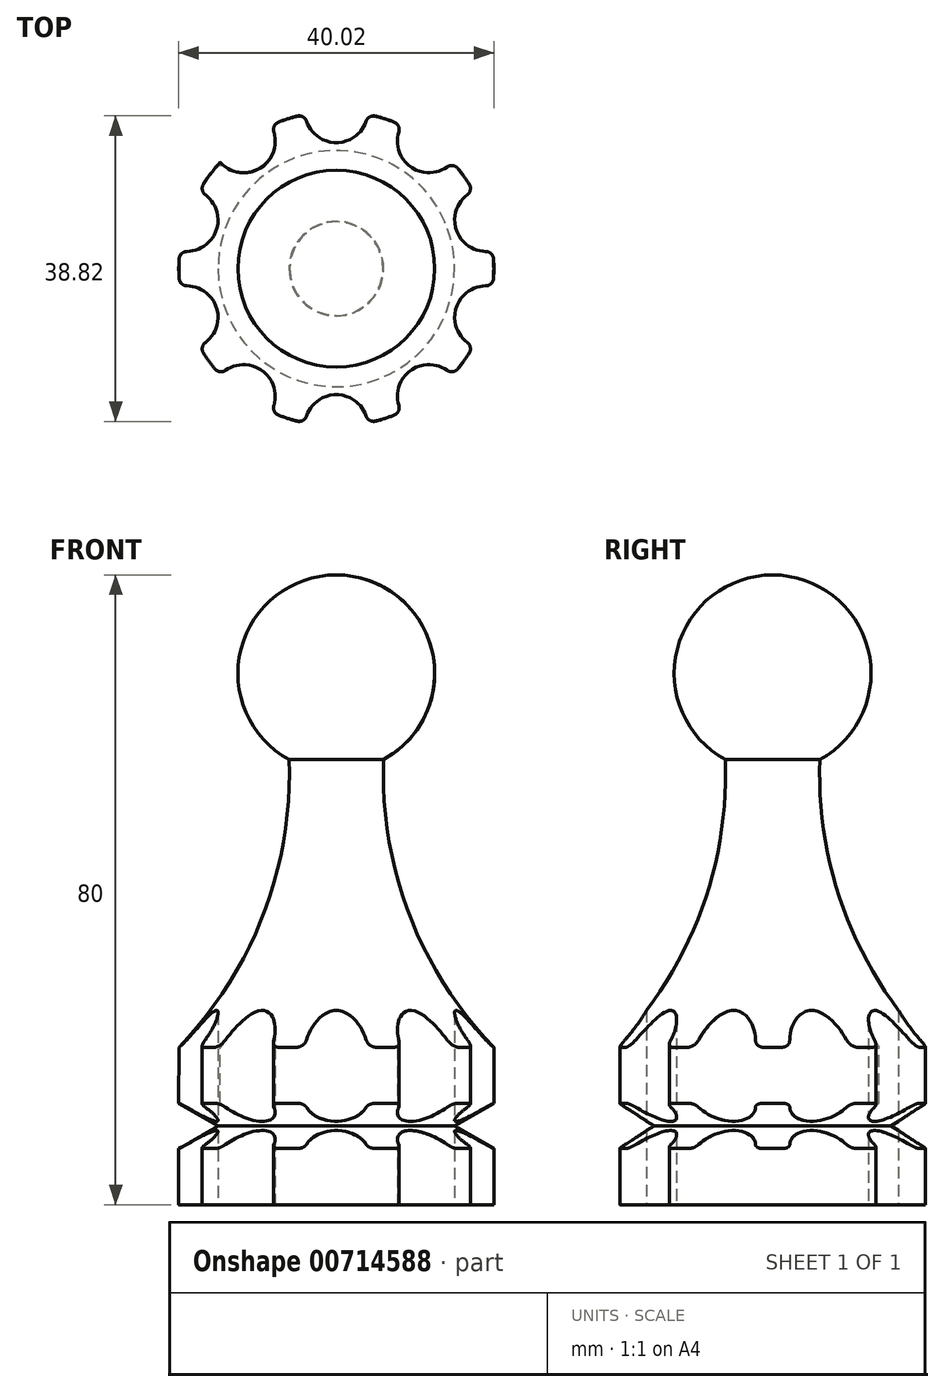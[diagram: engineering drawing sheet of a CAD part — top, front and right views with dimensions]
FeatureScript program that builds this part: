
annotation { "Feature Type Name" : "Feature", "Feature Type Description" : "" }
export const myFeature = defineFeature(function(context is Context, id is Id, definition is map)
    precondition{}
    {
        {
            var Q0;
            Q0=qCreatedBy(makeId("Front.planeOp"),FACE);
            var sketch = newSketch(context, id + "F0", { "sketchPlane" : qUnion([Q0])});
            skLineSegment(sketch, "E0", {"start": v(0, 0) * mm, "end": v(0, 80) * mm});
            skLineSegment(sketch, "E1", {"start": v(0, 0) * mm, "end": v(20, 0) * mm});
            skArc(sketch, "E2", {"start": v(6, 56.53) * mm, "mid": v(9.28, 36.84) * mm, "end": v(20, 20) * mm});
            skArc(sketch, "E3", {"start": v(6, 56.53) * mm, "mid": v(12.11, 70.6) * mm, "end": v(0, 80) * mm});
            skLineSegment(sketch, "E4", {"start": v(20, 0) * mm, "end": v(20, 7.12) * mm});
            skLineSegment(sketch, "E5", {"start": v(20, 7.12) * mm, "end": v(15, 10) * mm});
            skLineSegment(sketch, "E6", {"start": v(15, 10) * mm, "end": v(20, 12.9) * mm});
            skLineSegment(sketch, "E7", {"start": v(20, 12.9) * mm, "end": v(20, 20) * mm});
            skSolve(sketch);
        }
        {
            var Q0;
            Q0 = qSketchRegion(id + "F0", true);
            var Q1;
            Q1=sQuery(id+"F0.wireOp",EDGE,"E0");
            revolve(context, id + "F1", {"surfaceOperationType" : NewSurfaceOperationType.NEW, "entities" : qUnion([Q0]), "axis" : qUnion([Q1]), "revolveType" : RevolveType.FULL});
        }
        {
            var Q0;
            Q0=makeQuery(id+"F1.opRevolve","SWEPT_FACE",FACE,{"disambiguationData":[OSD([sQuery(id+"F0.wireOp",EDGE,"E1")])]});
            var sketch = newSketch(context, id + "F2", { "sketchPlane" : qUnion([Q0])});
            skCircle(sketch, "E8", {"center": v(0, 20) * mm, "radius": 4 * mm});
            skCircle(sketch, "E9.1.0", {"center": v(-11.76, 16.19) * mm, "radius": 4 * mm});
            skCircle(sketch, "E9.2.0", {"center": v(-19.03, 6.18) * mm, "radius": 4 * mm});
            skCircle(sketch, "E9.3.0", {"center": v(-19.03, -6.18) * mm, "radius": 4 * mm});
            skCircle(sketch, "E9.4.0", {"center": v(-11.76, -16.19) * mm, "radius": 4 * mm});
            skCircle(sketch, "E9.5.0", {"center": v(0, -20) * mm, "radius": 4 * mm});
            skCircle(sketch, "E9.6.0", {"center": v(11.76, -16.19) * mm, "radius": 4 * mm});
            skCircle(sketch, "E9.7.0", {"center": v(19.03, -6.18) * mm, "radius": 4 * mm});
            skCircle(sketch, "E9.8.0", {"center": v(19.03, 6.18) * mm, "radius": 4 * mm});
            skCircle(sketch, "E9.9.0", {"center": v(11.76, 16.19) * mm, "radius": 4 * mm});
            skPoint(sketch, "E9.center", {"position": v(0, 0) * mm});
            skSolve(sketch);
        }
        {
            var Q0;
            Q0 = qSketchRegion(id + "F2", true);
            extrude(context, id + "F3", {"entities" : qUnion([Q0]), "operationType" : NewBodyOperationType.REMOVE, "oppositeDirection" : true, "depth" : 25 * mm, "offsetDistance" : 25 * mm});
        }
        {
            var Q0;
            Q0=makeQuery(id+"F3.boolean.opBoolean","INTERSECT",EDGE,{"disambiguationData":[OD(1.0)],"derivedFrom":[makeQuery(id+"F1.opRevolve","SWEPT_FACE",FACE,{"disambiguationData":[OSD([sQuery(id+"F0.wireOp",EDGE,"E7")])]}),makeQuery(id+"F3.opExtrude","SWEPT_FACE",FACE,{"disambiguationData":[OSD([sQuery(id+"F2.wireOp",EDGE,"E9.1.0")])]})]});
            var Q1;
            Q1=makeQuery(id+"F3.boolean.opBoolean","INTERSECT",EDGE,{"disambiguationData":[OD(0.0)],"derivedFrom":[makeQuery(id+"F1.opRevolve","SWEPT_FACE",FACE,{"disambiguationData":[OSD([sQuery(id+"F0.wireOp",EDGE,"E7")])]}),makeQuery(id+"F3.opExtrude","SWEPT_FACE",FACE,{"disambiguationData":[OSD([sQuery(id+"F2.wireOp",EDGE,"E9.1.0")])]})]});
            var Q2;
            Q2=makeQuery(id+"F3.boolean.opBoolean","INTERSECT",EDGE,{"disambiguationData":[OD(1.0)],"derivedFrom":[makeQuery(id+"F1.opRevolve","SWEPT_FACE",FACE,{"disambiguationData":[OSD([sQuery(id+"F0.wireOp",EDGE,"E7")])]}),makeQuery(id+"F3.opExtrude","SWEPT_FACE",FACE,{"disambiguationData":[OSD([sQuery(id+"F2.wireOp",EDGE,"E8")])]})]});
            var Q3;
            Q3=makeQuery(id+"F3.boolean.opBoolean","INTERSECT",EDGE,{"disambiguationData":[OD(0.0)],"derivedFrom":[makeQuery(id+"F1.opRevolve","SWEPT_FACE",FACE,{"disambiguationData":[OSD([sQuery(id+"F0.wireOp",EDGE,"E7")])]}),makeQuery(id+"F3.opExtrude","SWEPT_FACE",FACE,{"disambiguationData":[OSD([sQuery(id+"F2.wireOp",EDGE,"E8")])]})]});
            var Q4;
            Q4=makeQuery(id+"F3.boolean.opBoolean","INTERSECT",EDGE,{"disambiguationData":[OD(0.0)],"derivedFrom":[makeQuery(id+"F1.opRevolve","SWEPT_FACE",FACE,{"disambiguationData":[OSD([sQuery(id+"F0.wireOp",EDGE,"E7")])]}),makeQuery(id+"F3.opExtrude","SWEPT_FACE",FACE,{"disambiguationData":[OSD([sQuery(id+"F2.wireOp",EDGE,"E9.9.0")])]})]});
            var Q5;
            Q5=makeQuery(id+"F3.boolean.opBoolean","INTERSECT",EDGE,{"disambiguationData":[OD(1.0)],"derivedFrom":[makeQuery(id+"F1.opRevolve","SWEPT_FACE",FACE,{"disambiguationData":[OSD([sQuery(id+"F0.wireOp",EDGE,"E7")])]}),makeQuery(id+"F3.opExtrude","SWEPT_FACE",FACE,{"disambiguationData":[OSD([sQuery(id+"F2.wireOp",EDGE,"E9.9.0")])]})]});
            var Q6;
            Q6=makeQuery(id+"F3.boolean.opBoolean","INTERSECT",EDGE,{"disambiguationData":[OD(1.0)],"derivedFrom":[makeQuery(id+"F1.opRevolve","SWEPT_FACE",FACE,{"disambiguationData":[OSD([sQuery(id+"F0.wireOp",EDGE,"E7")])]}),makeQuery(id+"F3.opExtrude","SWEPT_FACE",FACE,{"disambiguationData":[OSD([sQuery(id+"F2.wireOp",EDGE,"E9.8.0")])]})]});
            var Q7;
            Q7=makeQuery(id+"F3.boolean.opBoolean","INTERSECT",EDGE,{"disambiguationData":[OD(0.0)],"derivedFrom":[makeQuery(id+"F1.opRevolve","SWEPT_FACE",FACE,{"disambiguationData":[OSD([sQuery(id+"F0.wireOp",EDGE,"E7")])]}),makeQuery(id+"F3.opExtrude","SWEPT_FACE",FACE,{"disambiguationData":[OSD([sQuery(id+"F2.wireOp",EDGE,"E9.8.0")])]})]});
            var Q8;
            Q8=makeQuery(id+"F3.boolean.opBoolean","INTERSECT",EDGE,{"disambiguationData":[OD(1.0)],"derivedFrom":[makeQuery(id+"F1.opRevolve","SWEPT_FACE",FACE,{"disambiguationData":[OSD([sQuery(id+"F0.wireOp",EDGE,"E7")])]}),makeQuery(id+"F3.opExtrude","SWEPT_FACE",FACE,{"disambiguationData":[OSD([sQuery(id+"F2.wireOp",EDGE,"E9.7.0")])]})]});
            var Q9;
            Q9=makeQuery(id+"F3.boolean.opBoolean","INTERSECT",EDGE,{"disambiguationData":[OD(0.0)],"derivedFrom":[makeQuery(id+"F1.opRevolve","SWEPT_FACE",FACE,{"disambiguationData":[OSD([sQuery(id+"F0.wireOp",EDGE,"E7")])]}),makeQuery(id+"F3.opExtrude","SWEPT_FACE",FACE,{"disambiguationData":[OSD([sQuery(id+"F2.wireOp",EDGE,"E9.7.0")])]})]});
            var Q10;
            Q10=makeQuery(id+"F3.boolean.opBoolean","INTERSECT",EDGE,{"disambiguationData":[OD(1.0)],"derivedFrom":[makeQuery(id+"F1.opRevolve","SWEPT_FACE",FACE,{"disambiguationData":[OSD([sQuery(id+"F0.wireOp",EDGE,"E7")])]}),makeQuery(id+"F3.opExtrude","SWEPT_FACE",FACE,{"disambiguationData":[OSD([sQuery(id+"F2.wireOp",EDGE,"E9.6.0")])]})]});
            var Q11;
            Q11=makeQuery(id+"F3.boolean.opBoolean","INTERSECT",EDGE,{"disambiguationData":[OD(0.0)],"derivedFrom":[makeQuery(id+"F1.opRevolve","SWEPT_FACE",FACE,{"disambiguationData":[OSD([sQuery(id+"F0.wireOp",EDGE,"E7")])]}),makeQuery(id+"F3.opExtrude","SWEPT_FACE",FACE,{"disambiguationData":[OSD([sQuery(id+"F2.wireOp",EDGE,"E9.6.0")])]})]});
            var Q12;
            Q12=makeQuery(id+"F3.boolean.opBoolean","INTERSECT",EDGE,{"disambiguationData":[OD(1.0)],"derivedFrom":[makeQuery(id+"F1.opRevolve","SWEPT_FACE",FACE,{"disambiguationData":[OSD([sQuery(id+"F0.wireOp",EDGE,"E4")])]}),makeQuery(id+"F3.opExtrude","SWEPT_FACE",FACE,{"disambiguationData":[OSD([sQuery(id+"F2.wireOp",EDGE,"E9.1.0")])]})]});
            var Q13;
            Q13=makeQuery(id+"F3.boolean.opBoolean","INTERSECT",EDGE,{"disambiguationData":[OD(0.0)],"derivedFrom":[makeQuery(id+"F1.opRevolve","SWEPT_FACE",FACE,{"disambiguationData":[OSD([sQuery(id+"F0.wireOp",EDGE,"E4")])]}),makeQuery(id+"F3.opExtrude","SWEPT_FACE",FACE,{"disambiguationData":[OSD([sQuery(id+"F2.wireOp",EDGE,"E9.1.0")])]})]});
            var Q14;
            Q14=makeQuery(id+"F3.boolean.opBoolean","INTERSECT",EDGE,{"disambiguationData":[OD(0.0)],"derivedFrom":[makeQuery(id+"F1.opRevolve","SWEPT_FACE",FACE,{"disambiguationData":[OSD([sQuery(id+"F0.wireOp",EDGE,"E4")])]}),makeQuery(id+"F3.opExtrude","SWEPT_FACE",FACE,{"disambiguationData":[OSD([sQuery(id+"F2.wireOp",EDGE,"E8")])]})]});
            var Q15;
            Q15=makeQuery(id+"F3.boolean.opBoolean","INTERSECT",EDGE,{"disambiguationData":[OD(1.0)],"derivedFrom":[makeQuery(id+"F1.opRevolve","SWEPT_FACE",FACE,{"disambiguationData":[OSD([sQuery(id+"F0.wireOp",EDGE,"E4")])]}),makeQuery(id+"F3.opExtrude","SWEPT_FACE",FACE,{"disambiguationData":[OSD([sQuery(id+"F2.wireOp",EDGE,"E8")])]})]});
            var Q16;
            Q16=makeQuery(id+"F3.boolean.opBoolean","INTERSECT",EDGE,{"disambiguationData":[OD(0.0)],"derivedFrom":[makeQuery(id+"F1.opRevolve","SWEPT_FACE",FACE,{"disambiguationData":[OSD([sQuery(id+"F0.wireOp",EDGE,"E4")])]}),makeQuery(id+"F3.opExtrude","SWEPT_FACE",FACE,{"disambiguationData":[OSD([sQuery(id+"F2.wireOp",EDGE,"E9.9.0")])]})]});
            var Q17;
            Q17=makeQuery(id+"F3.boolean.opBoolean","INTERSECT",EDGE,{"disambiguationData":[OD(1.0)],"derivedFrom":[makeQuery(id+"F1.opRevolve","SWEPT_FACE",FACE,{"disambiguationData":[OSD([sQuery(id+"F0.wireOp",EDGE,"E4")])]}),makeQuery(id+"F3.opExtrude","SWEPT_FACE",FACE,{"disambiguationData":[OSD([sQuery(id+"F2.wireOp",EDGE,"E9.9.0")])]})]});
            var Q18;
            Q18=makeQuery(id+"F3.boolean.opBoolean","INTERSECT",EDGE,{"disambiguationData":[OD(1.0)],"derivedFrom":[makeQuery(id+"F1.opRevolve","SWEPT_FACE",FACE,{"disambiguationData":[OSD([sQuery(id+"F0.wireOp",EDGE,"E4")])]}),makeQuery(id+"F3.opExtrude","SWEPT_FACE",FACE,{"disambiguationData":[OSD([sQuery(id+"F2.wireOp",EDGE,"E9.8.0")])]})]});
            var Q19;
            Q19=makeQuery(id+"F3.boolean.opBoolean","INTERSECT",EDGE,{"disambiguationData":[OD(0.0)],"derivedFrom":[makeQuery(id+"F1.opRevolve","SWEPT_FACE",FACE,{"disambiguationData":[OSD([sQuery(id+"F0.wireOp",EDGE,"E4")])]}),makeQuery(id+"F3.opExtrude","SWEPT_FACE",FACE,{"disambiguationData":[OSD([sQuery(id+"F2.wireOp",EDGE,"E9.8.0")])]})]});
            var Q20;
            Q20=makeQuery(id+"F3.boolean.opBoolean","INTERSECT",EDGE,{"disambiguationData":[OD(1.0)],"derivedFrom":[makeQuery(id+"F1.opRevolve","SWEPT_FACE",FACE,{"disambiguationData":[OSD([sQuery(id+"F0.wireOp",EDGE,"E4")])]}),makeQuery(id+"F3.opExtrude","SWEPT_FACE",FACE,{"disambiguationData":[OSD([sQuery(id+"F2.wireOp",EDGE,"E9.7.0")])]})]});
            var Q21;
            Q21=makeQuery(id+"F3.boolean.opBoolean","INTERSECT",EDGE,{"disambiguationData":[OD(0.0)],"derivedFrom":[makeQuery(id+"F1.opRevolve","SWEPT_FACE",FACE,{"disambiguationData":[OSD([sQuery(id+"F0.wireOp",EDGE,"E4")])]}),makeQuery(id+"F3.opExtrude","SWEPT_FACE",FACE,{"disambiguationData":[OSD([sQuery(id+"F2.wireOp",EDGE,"E9.7.0")])]})]});
            var Q22;
            Q22=makeQuery(id+"F3.boolean.opBoolean","INTERSECT",EDGE,{"disambiguationData":[OD(1.0)],"derivedFrom":[makeQuery(id+"F1.opRevolve","SWEPT_FACE",FACE,{"disambiguationData":[OSD([sQuery(id+"F0.wireOp",EDGE,"E4")])]}),makeQuery(id+"F3.opExtrude","SWEPT_FACE",FACE,{"disambiguationData":[OSD([sQuery(id+"F2.wireOp",EDGE,"E9.6.0")])]})]});
            var Q23;
            Q23=makeQuery(id+"F3.boolean.opBoolean","INTERSECT",EDGE,{"disambiguationData":[OD(0.0)],"derivedFrom":[makeQuery(id+"F1.opRevolve","SWEPT_FACE",FACE,{"disambiguationData":[OSD([sQuery(id+"F0.wireOp",EDGE,"E4")])]}),makeQuery(id+"F3.opExtrude","SWEPT_FACE",FACE,{"disambiguationData":[OSD([sQuery(id+"F2.wireOp",EDGE,"E9.6.0")])]})]});
            var Q24;
            Q24=makeQuery(id+"F3.boolean.opBoolean","INTERSECT",EDGE,{"disambiguationData":[OD(0.0)],"derivedFrom":[makeQuery(id+"F1.opRevolve","SWEPT_FACE",FACE,{"disambiguationData":[OSD([sQuery(id+"F0.wireOp",EDGE,"E4")])]}),makeQuery(id+"F3.opExtrude","SWEPT_FACE",FACE,{"disambiguationData":[OSD([sQuery(id+"F2.wireOp",EDGE,"E9.5.0")])]})]});
            var Q25;
            Q25=makeQuery(id+"F3.boolean.opBoolean","INTERSECT",EDGE,{"disambiguationData":[OD(1.0)],"derivedFrom":[makeQuery(id+"F1.opRevolve","SWEPT_FACE",FACE,{"disambiguationData":[OSD([sQuery(id+"F0.wireOp",EDGE,"E4")])]}),makeQuery(id+"F3.opExtrude","SWEPT_FACE",FACE,{"disambiguationData":[OSD([sQuery(id+"F2.wireOp",EDGE,"E9.5.0")])]})]});
            var Q26;
            Q26=makeQuery(id+"F3.boolean.opBoolean","INTERSECT",EDGE,{"disambiguationData":[OD(1.0)],"derivedFrom":[makeQuery(id+"F1.opRevolve","SWEPT_FACE",FACE,{"disambiguationData":[OSD([sQuery(id+"F0.wireOp",EDGE,"E7")])]}),makeQuery(id+"F3.opExtrude","SWEPT_FACE",FACE,{"disambiguationData":[OSD([sQuery(id+"F2.wireOp",EDGE,"E9.3.0")])]})]});
            var Q27;
            Q27=makeQuery(id+"F3.boolean.opBoolean","INTERSECT",EDGE,{"disambiguationData":[OD(0.0)],"derivedFrom":[makeQuery(id+"F1.opRevolve","SWEPT_FACE",FACE,{"disambiguationData":[OSD([sQuery(id+"F0.wireOp",EDGE,"E7")])]}),makeQuery(id+"F3.opExtrude","SWEPT_FACE",FACE,{"disambiguationData":[OSD([sQuery(id+"F2.wireOp",EDGE,"E9.3.0")])]})]});
            var Q28;
            Q28=makeQuery(id+"F3.boolean.opBoolean","INTERSECT",EDGE,{"disambiguationData":[OD(1.0)],"derivedFrom":[makeQuery(id+"F1.opRevolve","SWEPT_FACE",FACE,{"disambiguationData":[OSD([sQuery(id+"F0.wireOp",EDGE,"E7")])]}),makeQuery(id+"F3.opExtrude","SWEPT_FACE",FACE,{"disambiguationData":[OSD([sQuery(id+"F2.wireOp",EDGE,"E9.2.0")])]})]});
            var Q29;
            Q29=makeQuery(id+"F3.boolean.opBoolean","INTERSECT",EDGE,{"disambiguationData":[OD(0.0)],"derivedFrom":[makeQuery(id+"F1.opRevolve","SWEPT_FACE",FACE,{"disambiguationData":[OSD([sQuery(id+"F0.wireOp",EDGE,"E7")])]}),makeQuery(id+"F3.opExtrude","SWEPT_FACE",FACE,{"disambiguationData":[OSD([sQuery(id+"F2.wireOp",EDGE,"E9.2.0")])]})]});
            var Q30;
            Q30=makeQuery(id+"F3.boolean.opBoolean","INTERSECT",EDGE,{"disambiguationData":[OD(0.0)],"derivedFrom":[makeQuery(id+"F1.opRevolve","SWEPT_FACE",FACE,{"disambiguationData":[OSD([sQuery(id+"F0.wireOp",EDGE,"E7")])]}),makeQuery(id+"F3.opExtrude","SWEPT_FACE",FACE,{"disambiguationData":[OSD([sQuery(id+"F2.wireOp",EDGE,"E9.5.0")])]})]});
            var Q31;
            Q31=makeQuery(id+"F3.boolean.opBoolean","INTERSECT",EDGE,{"disambiguationData":[OD(1.0)],"derivedFrom":[makeQuery(id+"F1.opRevolve","SWEPT_FACE",FACE,{"disambiguationData":[OSD([sQuery(id+"F0.wireOp",EDGE,"E7")])]}),makeQuery(id+"F3.opExtrude","SWEPT_FACE",FACE,{"disambiguationData":[OSD([sQuery(id+"F2.wireOp",EDGE,"E9.4.0")])]})]});
            var Q32;
            Q32=makeQuery(id+"F3.boolean.opBoolean","INTERSECT",EDGE,{"disambiguationData":[OD(1.0)],"derivedFrom":[makeQuery(id+"F1.opRevolve","SWEPT_FACE",FACE,{"disambiguationData":[OSD([sQuery(id+"F0.wireOp",EDGE,"E7")])]}),makeQuery(id+"F3.opExtrude","SWEPT_FACE",FACE,{"disambiguationData":[OSD([sQuery(id+"F2.wireOp",EDGE,"E9.5.0")])]})]});
            var Q33;
            Q33=makeQuery(id+"F3.boolean.opBoolean","INTERSECT",EDGE,{"disambiguationData":[OD(1.0)],"derivedFrom":[makeQuery(id+"F1.opRevolve","SWEPT_FACE",FACE,{"disambiguationData":[OSD([sQuery(id+"F0.wireOp",EDGE,"E4")])]}),makeQuery(id+"F3.opExtrude","SWEPT_FACE",FACE,{"disambiguationData":[OSD([sQuery(id+"F2.wireOp",EDGE,"E9.2.0")])]})]});
            var Q34;
            Q34=makeQuery(id+"F3.boolean.opBoolean","INTERSECT",EDGE,{"disambiguationData":[OD(0.0)],"derivedFrom":[makeQuery(id+"F1.opRevolve","SWEPT_FACE",FACE,{"disambiguationData":[OSD([sQuery(id+"F0.wireOp",EDGE,"E4")])]}),makeQuery(id+"F3.opExtrude","SWEPT_FACE",FACE,{"disambiguationData":[OSD([sQuery(id+"F2.wireOp",EDGE,"E9.3.0")])]})]});
            var Q35;
            Q35=makeQuery(id+"F3.boolean.opBoolean","INTERSECT",EDGE,{"disambiguationData":[OD(1.0)],"derivedFrom":[makeQuery(id+"F1.opRevolve","SWEPT_FACE",FACE,{"disambiguationData":[OSD([sQuery(id+"F0.wireOp",EDGE,"E4")])]}),makeQuery(id+"F3.opExtrude","SWEPT_FACE",FACE,{"disambiguationData":[OSD([sQuery(id+"F2.wireOp",EDGE,"E9.3.0")])]})]});
            var Q36;
            Q36=makeQuery(id+"F3.boolean.opBoolean","INTERSECT",EDGE,{"disambiguationData":[OD(0.0)],"derivedFrom":[makeQuery(id+"F1.opRevolve","SWEPT_FACE",FACE,{"disambiguationData":[OSD([sQuery(id+"F0.wireOp",EDGE,"E4")])]}),makeQuery(id+"F3.opExtrude","SWEPT_FACE",FACE,{"disambiguationData":[OSD([sQuery(id+"F2.wireOp",EDGE,"E9.2.0")])]})]});
            var Q37;
            Q37=makeQuery(id+"F3.boolean.opBoolean","INTERSECT",EDGE,{"disambiguationData":[OD(0.0)],"derivedFrom":[makeQuery(id+"F1.opRevolve","SWEPT_FACE",FACE,{"disambiguationData":[OSD([sQuery(id+"F0.wireOp",EDGE,"E4")])]}),makeQuery(id+"F3.opExtrude","SWEPT_FACE",FACE,{"disambiguationData":[OSD([sQuery(id+"F2.wireOp",EDGE,"E9.4.0")])]})]});
            var Q38;
            Q38=makeQuery(id+"F3.boolean.opBoolean","INTERSECT",EDGE,{"disambiguationData":[OD(1.0)],"derivedFrom":[makeQuery(id+"F1.opRevolve","SWEPT_FACE",FACE,{"disambiguationData":[OSD([sQuery(id+"F0.wireOp",EDGE,"E4")])]}),makeQuery(id+"F3.opExtrude","SWEPT_FACE",FACE,{"disambiguationData":[OSD([sQuery(id+"F2.wireOp",EDGE,"E9.4.0")])]})]});
            fillet(context, id + "F4", {"entities" : qUnion([Q0, Q1, Q2, Q3, Q4, Q5, Q6, Q7, Q8, Q9, Q10, Q11, Q12, Q13, Q14, Q15, Q16, Q17, Q18, Q19, Q20, Q21, Q22, Q23, Q24, Q25, Q26, Q27, Q28, Q29, Q30, Q31, Q32, Q33, Q34, Q35, Q36, Q37, Q38]), "radius" : 1 * mm, "tangentPropagation" : true, "allowEdgeOverflow" : false});
        }
    });
